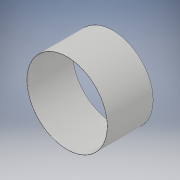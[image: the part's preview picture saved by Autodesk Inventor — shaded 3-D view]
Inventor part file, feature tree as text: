
AUTODESK INVENTOR PART (.ipt)
format: ipt  version: 2019 (Build 230136000, 136)  size: 103,936 bytes
history: native  units: mm
features: extrude x2, sketch x2
ambient origin geometry x8: Origin, YZ Plane, XZ Plane, XY Plane, X Axis, Y Axis, Z Axis, Center Point
bodies: Solid1 (feature_tree)
feature tree (4):
  extrude  "Extrusion1"  Depth=115.1mm TaperAngle=0.0deg
  extrude  "Extrusion2"  Depth=11.51mm TaperAngle=0.0deg
  sketch  "Sketch1"  dims[d0=202.7mm d1=115.1mm d2=0.0mm]
  sketch  "Sketch2"  dims[d3=201.7mm d4=11.51mm d5=0.0mm]
